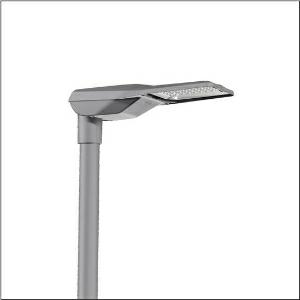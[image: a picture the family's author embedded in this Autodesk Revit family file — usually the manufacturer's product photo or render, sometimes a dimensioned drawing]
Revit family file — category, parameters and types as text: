
# Revit family: streetlight_sl_21_iq_mini___stw1_0a_5xe2e61g08hb_1142
name_source: partatom
category: Lighting Fixtures
units: mm (PartAtom-declared; Revit-internal decimal feet)

## family parameters
Cut with Voids When Loaded = No
Host = Face
Light Source = No
Part Type = Normal
Room Calculation Point = No
Round Connector Dimension = Use Diameter
Shared = No

## types (1)
- --- (1 x LED, 8480 lm, 70.9 W, 2700K)
    Apparent Load = 71 VA
    CIE Flux Codes = 38 75 98 100 100
    Color Rendering = 70
    Color Temperature = 2700K
    Default Elevation = 1800 mm
    Description = Streetlight SL 21 iQ mini, mast luminaire, primary light control with lens, of PMMA, primary optical cover: cover, of toughened safety glass, transparent, light distribution: STW1.0a, light emission: direct distribution, primary light characteristic: asymmetric, installation type: post-top, side-entry, LED, High Power LED, rated luminous flux: 8.480lm, luminous efficacy: 120lm/W, light colour: 727, colour temperature: 2700K, control gear: iQ Street-Remote, control: Street-Remote, Auto-Match, Temp-Guard, Lumen-Switch, Night-Set, Smart-Wire, Light-Fading, Desk-Remote (wireless, voltage-free reading and setting of iQ features in the workshop via application-optimized NFC function/RFID function), optimised constant luminous flux control (CLO 2.0), pre-setting: linear dimming characteristic, mains connection: 220..240V, AC, 50/60Hz, start of lifetime: 71W, end of service life: 75W, reduction: 31W, luminaire housing, of diecast aluminium, powder-coated, SITECO metallic grey (DB 702S), corrosivity category C5 high according to DIN EN ISO 12944, please order mast flange separately, inclination adjustable: 0°, 5°, 10°, 15°, sealing non-destructively replaceable, multi-level sealing system, length: 628mm, width: 235mm, height: 110mm, mast flange for spigot size: 42mm (side-entry): 5XC10008XM4, 60/48mm (side-entry/post-top): 5XC10108XM2, 76/60mm (side-entry/post-top): 5XC10108XM1, mounting height: 4..8m, protection rating (complete): IP66, insulation class (complete): insulation class II (safety insulation), certification: CE, ENEC, ENEC+, VDE, impact resistance: IK10, permissible operating ambient temperature for outdoor applications: -40..+50°C, standard-compliant lighting for roads and squares, packaging unit: 1 piece

Light Distribution: STW1.0a
    Height = 110 mm
    Lamp = 1 x LED
    Lamp Light Flux = 8480 lm
    Lamp Power = 70.9 W
    Lamp count = 1
    Length = 625 mm
    Luminous efficacy = 120 lm/W
    Manufacturer = Siteco
    ModVariant = No
    Model = 5XE2E61G08HB
    Number of Poles = 1
    OnlyDefault = Yes
    Power Factor = 1
    Product Name = Streetlight SL 21 iQ mini | STW1.0a
    Product group = mast luminaire | pylon top
    ProductGroupID = 6100
    Protection Class = Protection class II
    Protection Degree = IP 66
    RLX_Detail_Level = 1
    RLX_Emergency_Light_Flux = 0 lm
    RLX_Emergency_Type = 0
    RLX_Emergency_Type_DB = No
    RlxData = <blob elided: 26317 chars, md5=f49dc115>
    Socket = socket
    Standby Power = 0 W
    System Light Flux = 8480 lm
    System Power = 71 W
    Type Comments = factory setting: luminous flux: 100 % | dim-lin: 254 | 711 mA
    Type Image = l_1003519.jpg
    URL = http://relux.com
    VarID = @adj_157375
    Voltage = 0 V
    Weight = 0.00 kg
    Width = 234 mm

## geometry (parser evidence)
native form markers: Blend x4, Sweep x12
no freeform markers — native parametric forms only
